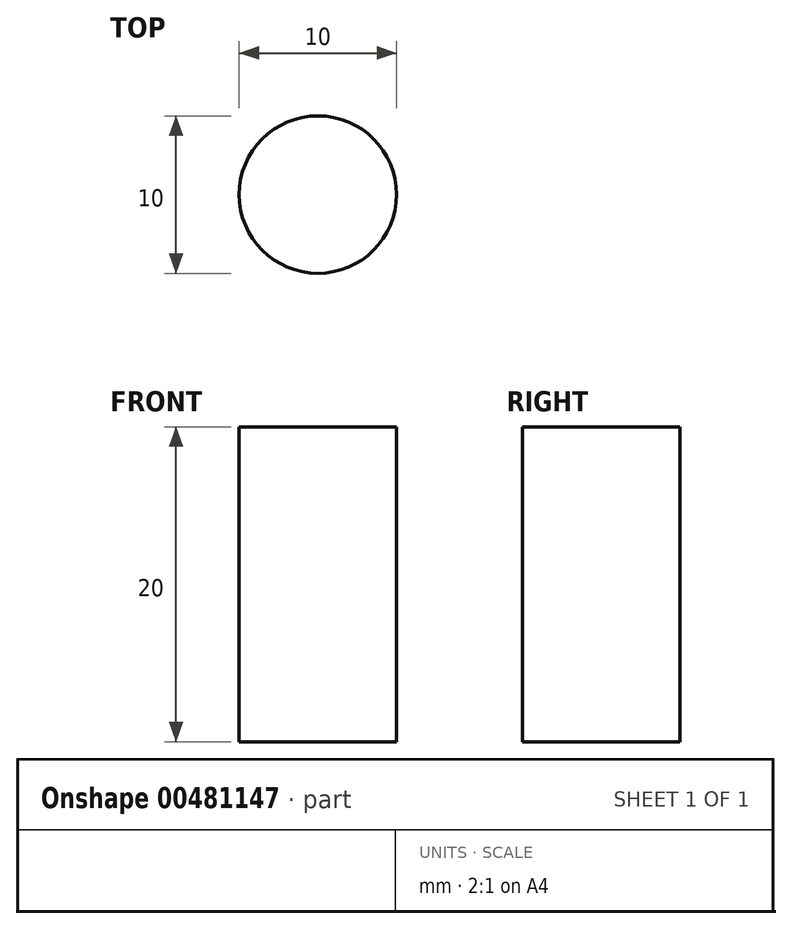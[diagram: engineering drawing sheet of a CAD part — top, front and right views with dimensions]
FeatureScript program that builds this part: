
annotation { "Feature Type Name" : "Feature", "Feature Type Description" : "" }
export const myFeature = defineFeature(function(context is Context, id is Id, definition is map)
    precondition{}
    {
        {
            assignVariable(context, id + "F0", {"name" : "height", "anyValue" : 20});
        }
        {
            var Q0;
            Q0=qCreatedBy(makeId("Top.planeOp"),FACE);
            var sketch = newSketch(context, id + "F1", { "sketchPlane" : qUnion([Q0])});
            skCircle(sketch, "E0", {"center": v(0, 0) * mm, "radius": 5 * mm});
            skSolve(sketch);
        }
        {
            var Q0;
            Q0=makeQuery(id+"F1.imprint","IMPRINT",FACE,{"disambiguationData":[TD([[makeQuery(id+"F1.imprint","IMPRINT",EDGE,{"derivedFrom":sQuery(id+"F1.wireOp",EDGE,"E0")}),1.0]])]});
            extrude(context, id + "F2", {"entities" : qUnion([Q0]), "depth" : (getVariable(context, 'height')) * mm});
        }
    });
